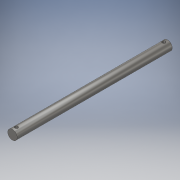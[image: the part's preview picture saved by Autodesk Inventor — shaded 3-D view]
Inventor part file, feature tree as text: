
AUTODESK INVENTOR PART (.ipt)
format: ipt  version: 2017 (Build 210142000, 142)  size: 109,568 bytes
history: native  units: in
note: dims shown in document units (in); Inventor stores cm internally (conversion verified against a paired STEP export)
features: extrude x2, sketch x2
ambient origin geometry x8: Origin, YZ Plane, XZ Plane, XY Plane, X Axis, Y Axis, Z Axis, Center Point
bodies: Solid1 (feature_tree)
feature tree (4):
  extrude  "Extrusion1"  Depth=5.125in TaperAngle=0.0deg
  extrude  "Extrusion2"  Depth=0.125in
  sketch  "Sketch1"  dims[d0=0.3115in d1=5.125in d2=0.0in]
  sketch  "Sketch2"  dims[d3=0.104in d4=0.104in d5=0.125in d6=0.125in d7=1.0in d8=0.0in]
